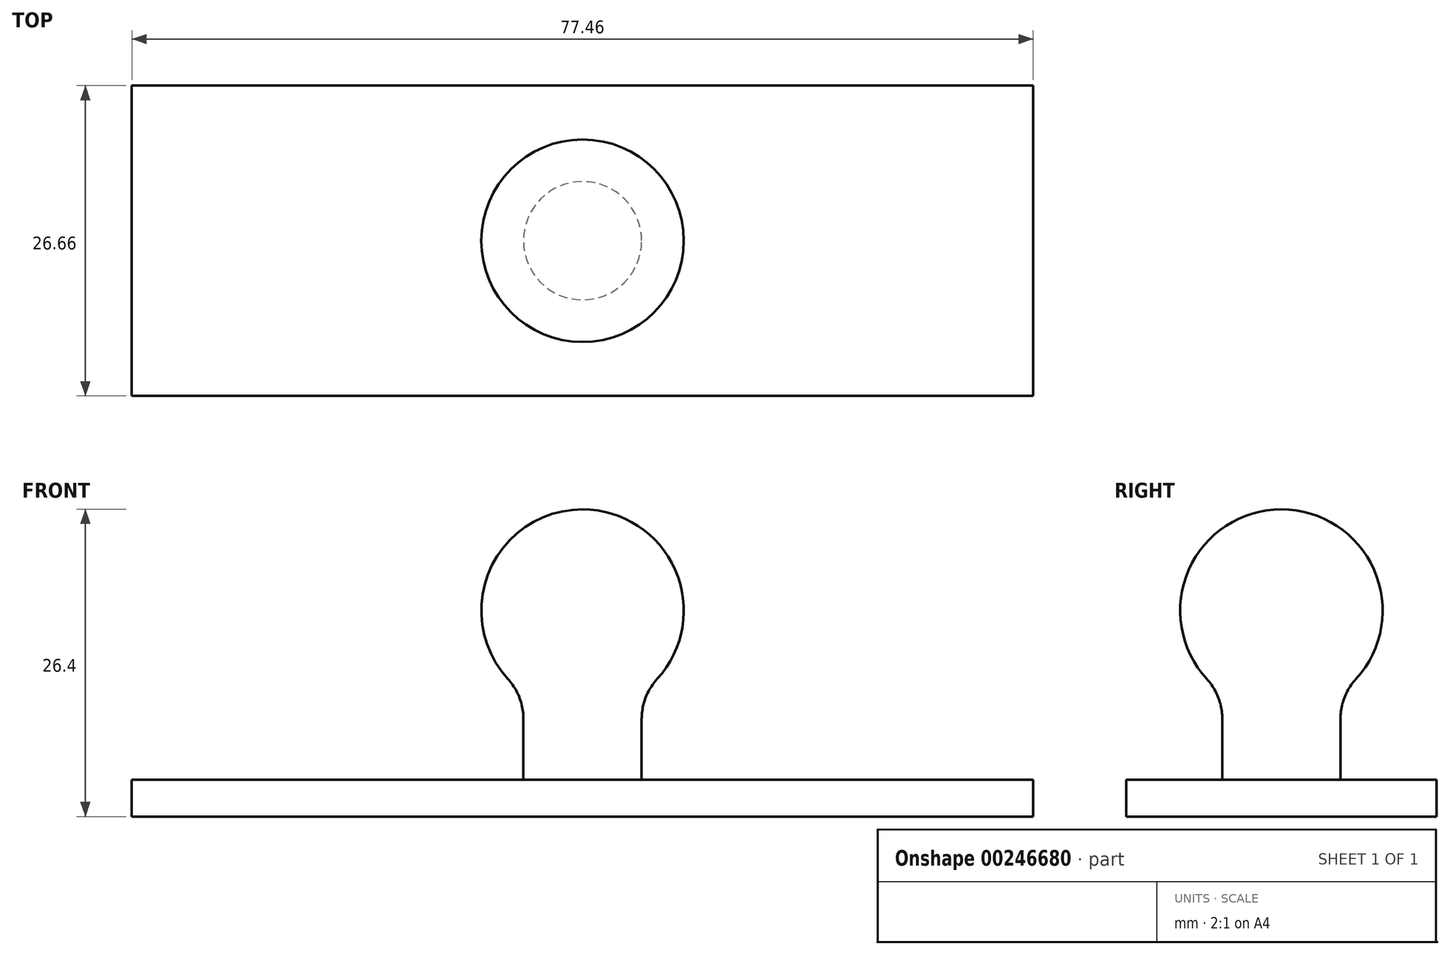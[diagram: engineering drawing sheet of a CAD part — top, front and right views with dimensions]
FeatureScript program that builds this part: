
annotation { "Feature Type Name" : "Feature", "Feature Type Description" : "" }
export const myFeature = defineFeature(function(context is Context, id is Id, definition is map)
    precondition{}
    {
        {
            var Q0;
            Q0=qCreatedBy(makeId("Top.planeOp"),FACE);
            var sketch = newSketch(context, id + "F0", { "sketchPlane" : qUnion([Q0])});
            skLineSegment(sketch, "E0.bottom", {"start": v(38.73, 13.33) * mm, "end": v(-38.73, 13.33) * mm});
            skLineSegment(sketch, "E0.top", {"start": v(38.73, -13.34) * mm, "end": v(-38.73, -13.34) * mm});
            skLineSegment(sketch, "E0.left", {"start": v(38.73, 13.33) * mm, "end": v(38.73, -13.34) * mm});
            skLineSegment(sketch, "E0.right", {"start": v(-38.73, 13.33) * mm, "end": v(-38.73, -13.34) * mm});
            skPoint(sketch, "E0.middle", {"position": v(0, 0) * mm});
            skSolve(sketch);
        }
        {
            var Q0;
            Q0=qSketchRegion(id+"F0",true);
            extrude(context, id + "F1", {"entities" : qUnion([Q0]), "depth" : 3.17 * mm});
        }
        {
            var Q0;
            Q0=makeQuery(id+"F1.opExtrude","CAP_FACE",FACE,{"disambiguationData":[OSD([sQuery(id+"F0.wireOp",EDGE,"E0.bottom"),sQuery(id+"F0.wireOp",EDGE,"E0.top"),sQuery(id+"F0.wireOp",EDGE,"E0.left"),sQuery(id+"F0.wireOp",EDGE,"E0.right")])],"isStart":false});
            var sketch = newSketch(context, id + "F2", { "sketchPlane" : qUnion([Q0])});
            skCircle(sketch, "E1", {"center": v(0, 0) * mm, "radius": 5.08 * mm});
            skSolve(sketch);
        }
        {
            var Q0;
            Q0=qSketchRegion(id+"F2",true);
            extrude(context, id + "F3", {"entities" : qUnion([Q0]), "operationType" : NewBodyOperationType.ADD, "depth" : 14.53 * mm});
        }
        {
            var Q0;
            Q0=qCreatedBy(makeId("Front.planeOp"),FACE);
            var sketch = newSketch(context, id + "F4", { "sketchPlane" : qUnion([Q0])});
            skLineSegment(sketch, "E2.0", {"start": v(-5.08, 17.7) * mm, "end": v(5.08, 17.7) * mm, "construction": true});
            skPoint(sketch, "E3", {"position": v(0, 17.7) * mm});
            skCircle(sketch, "E4", {"center": v(0, 17.7) * mm, "radius": 8.7 * mm, "construction": true});
            skPoint(sketch, "E5", {"position": v(0, 26.4) * mm});
            skPoint(sketch, "E6", {"position": v(0, 9) * mm});
            skPoint(sketch, "E7", {"position": v(8.7, 17.7) * mm});
            skArc(sketch, "E8", {"start": v(0, 9) * mm, "mid": v(8.7, 17.7) * mm, "end": v(0, 26.4) * mm});
            skLineSegment(sketch, "E9", {"start": v(0, 26.4) * mm, "end": v(0, 9) * mm});
            skSolve(sketch);
        }
        {
            var Q0;
            Q0=qSketchRegion(id+"F4",true);
            var Q1;
            Q1=sQuery(id+"F4.wireOp",EDGE,"E9");
            revolve(context, id + "F5", {"operationType" : NewBodyOperationType.ADD, "entities" : qUnion([Q0]), "axis" : qUnion([Q1]), "revolveType" : RevolveType.FULL});
        }
        {
            var Q0;
            Q0=makeQuery(id+"F3.opExtrude","CAP_EDGE",EDGE,{"disambiguationData":[OSD([sQuery(id+"F2.wireOp",EDGE,"E1")])],"isStart":true});
            var Q1;
            Q1=makeQuery(id+"F5.boolean.opBoolean","INTERSECT",EDGE,{"derivedFrom":[makeQuery(id+"F3.opExtrude","SWEPT_FACE",FACE,{"disambiguationData":[OSD([sQuery(id+"F2.wireOp",EDGE,"E1")])]}),makeQuery(id+"F5.opRevolve","SWEPT_FACE",FACE,{"disambiguationData":[OSD([sQuery(id+"F4.wireOp",EDGE,"E8")])]})]});
            fillet(context, id + "F6", {"entities" : qUnion([Q0, Q1]), "radius" : 5.08 * mm, "tangentPropagation" : true, "allowEdgeOverflow" : false});
        }
    });
